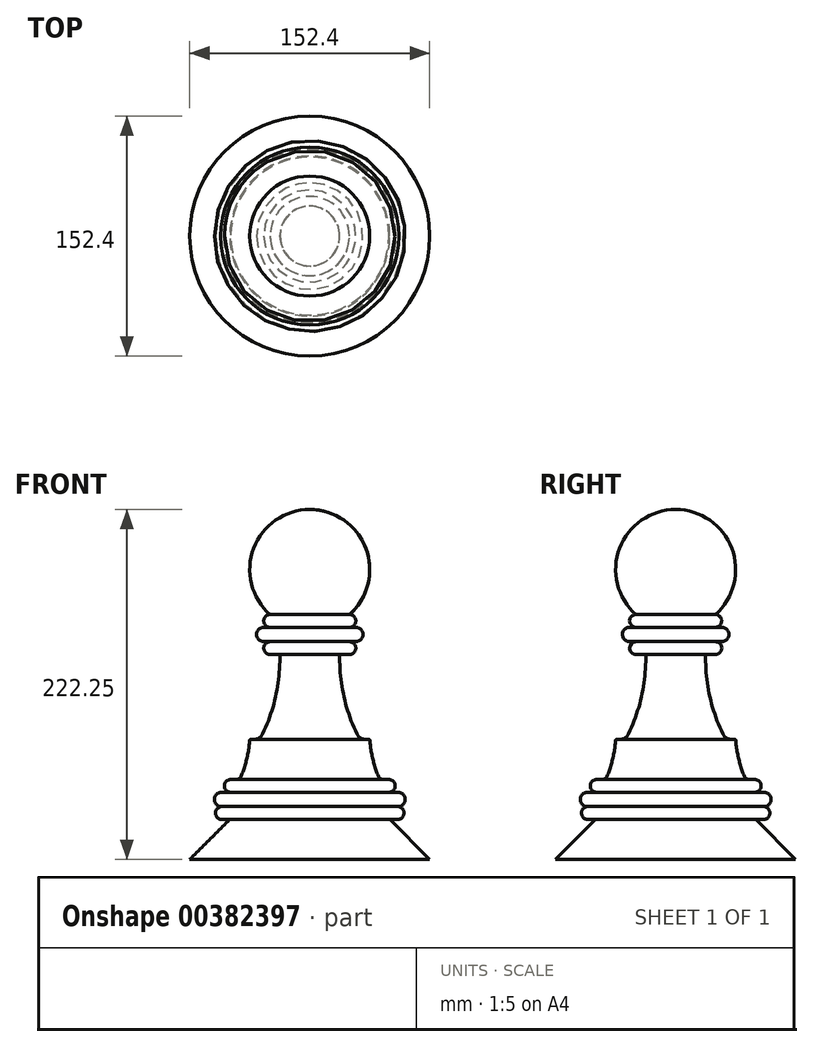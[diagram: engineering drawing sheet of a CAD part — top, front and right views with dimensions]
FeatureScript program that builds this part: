
annotation { "Feature Type Name" : "Feature", "Feature Type Description" : "" }
export const myFeature = defineFeature(function(context is Context, id is Id, definition is map)
    precondition{}
    {
        {
            var Q0;
            Q0=qCreatedBy(makeId("Front.planeOp"),FACE);
            var sketch = newSketch(context, id + "F0", { "sketchPlane" : qUnion([Q0])});
            skLineSegment(sketch, "E0", {"start": v(50.8, 25.4) * mm, "end": v(76.2, 0) * mm});
            skLineSegment(sketch, "E1", {"start": v(37.72, 76.2) * mm, "end": v(35.66, 76.2) * mm});
            skLineSegment(sketch, "E2", {"start": v(50.8, 25.4) * mm, "end": v(54.86, 25.4) * mm});
            skLineSegment(sketch, "E3", {"start": v(50.21, 50.8) * mm, "end": v(46.55, 50.8) * mm});
            skArc(sketch, "E4", {"start": v(54.86, 25.4) * mm, "mid": v(59.77, 28.63) * mm, "end": v(56.54, 33.53) * mm});
            skPoint(sketch, "E5.orphan", {"position": v(63.5, 50.8) * mm});
            skArc(sketch, "E6", {"start": v(38.13, 75.82) * mm, "mid": v(39.97, 64.08) * mm, "end": v(43.6, 52.77) * mm});
            skLineSegment(sketch, "E7", {"start": v(25.2, 130.18) * mm, "end": v(19.05, 130.18) * mm});
            skArc(sketch, "E8", {"start": v(19.05, 130.17) * mm, "mid": v(21.5, 104.34) * mm, "end": v(29.94, 79.8) * mm});
            skArc(sketch, "E9", {"start": v(29.26, 138.3) * mm, "mid": v(33.83, 142.88) * mm, "end": v(29.26, 147.45) * mm});
            skLineSegment(sketch, "E10", {"start": v(29.26, 147.45) * mm, "end": v(25.2, 147.45) * mm});
            skLineSegment(sketch, "E11", {"start": v(29.26, 138.3) * mm, "end": v(25.2, 138.3) * mm});
            skArc(sketch, "E12", {"start": v(25.2, 147.45) * mm, "mid": v(29.26, 151.5) * mm, "end": v(25.2, 155.57) * mm});
            skArc(sketch, "E13", {"start": v(25.2, 130.18) * mm, "mid": v(29.26, 134.24) * mm, "end": v(25.2, 138.3) * mm});
            skArc(sketch, "E14", {"start": v(25.2, 155.57) * mm, "mid": v(35.64, 197.62) * mm, "end": v(0, 222.25) * mm});
            skPoint(sketch, "E15.orphan", {"position": v(29.26, 155.58) * mm});
            skPoint(sketch, "E16.end.orphan", {"position": v(29.26, 130.18) * mm});
            skLineSegment(sketch, "E17", {"start": v(0, 0) * mm, "end": v(0, 222.25) * mm});
            skLineSegment(sketch, "E18", {"start": v(0, 0) * mm, "end": v(76.2, 0) * mm});
            skPoint(sketch, "E19.visualSharp", {"position": v(31.75, 76.2) * mm});
            skArc(sketch, "E19.filletArc", {"start": v(29.94, 79.8) * mm, "mid": v(32.28, 77.17) * mm, "end": v(35.66, 76.2) * mm});
            skPoint(sketch, "E20.visualSharp", {"position": v(44.45, 50.8) * mm});
            skArc(sketch, "E20.filletArc", {"start": v(43.6, 52.77) * mm, "mid": v(44.78, 51.34) * mm, "end": v(46.55, 50.8) * mm});
            skPoint(sketch, "E21.visualSharp", {"position": v(38.1, 76.2) * mm});
            skArc(sketch, "E21.filletArc", {"start": v(38.13, 75.82) * mm, "mid": v(38, 76.09) * mm, "end": v(37.72, 76.2) * mm});
            skPoint(sketch, "E22.endSnap0", {"position": v(58.93, 46.74) * mm});
            skArc(sketch, "E23", {"start": v(50.21, 42.67) * mm, "mid": v(54.27, 46.74) * mm, "end": v(50.21, 50.8) * mm});
            skLineSegment(sketch, "E24", {"start": v(56.54, 42.67) * mm, "end": v(50.21, 42.67) * mm});
            skPoint(sketch, "E25.endSnap0", {"position": v(65.18, 38.1) * mm});
            skArc(sketch, "E26", {"start": v(56.54, 33.53) * mm, "mid": v(60.63, 38.1) * mm, "end": v(56.54, 42.67) * mm});
            skPoint(sketch, "E27.orphan", {"position": v(60.6, 42.67) * mm});
            skPoint(sketch, "E28.start.orphan", {"position": v(60.6, 33.53) * mm});
            skPoint(sketch, "E25.start.orphan", {"position": v(60.6, 38.1) * mm});
            skSolve(sketch);
        }
        {
            var Q0;
            Q0 = qSketchRegion(id + "F0", true);
            var Q1;
            Q1=sQuery(id+"F0.wireOp",EDGE,"E17");
            revolve(context, id + "F1", {"entities" : qUnion([Q0]), "axis" : qUnion([Q1]), "revolveType" : RevolveType.FULL});
        }
    });
